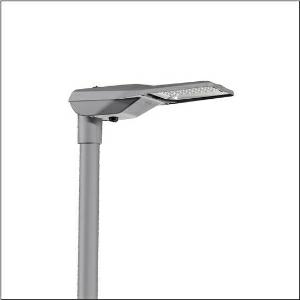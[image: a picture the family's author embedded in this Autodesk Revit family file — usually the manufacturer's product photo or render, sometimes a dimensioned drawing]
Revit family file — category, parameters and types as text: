
# Revit family: streetlight_sl_21_iq_mini___st0_8a_5xe2c31y08gb_e7ef
name_source: partatom
category: Lighting Fixtures
units: mm (PartAtom-declared; Revit-internal decimal feet)

## family parameters
Cut with Voids When Loaded = No
Host = Face
Light Source = No
Part Type = Normal
Room Calculation Point = No
Round Connector Dimension = Use Diameter
Shared = No

## types (1)
- --- (1 x LED, 5990 lm, 39.8 W, 3000K)
    Apparent Load = 40 VA
    CIE Flux Codes = 38 75 97 100 100
    Color Rendering = 70
    Color Temperature = 3000K
    Default Elevation = 1800 mm
    Description = Streetlight SL 21 iQ mini, mast luminaire, primary light control with lens, of PMMA, primary optical cover: cover, of toughened safety glass, transparent, light distribution: ST0.8a, light emission: direct distribution, primary light characteristic: asymmetric, installation type: post-top, side-entry, LED, High Power LED, rated luminous flux: 5.990lm, luminous efficacy: 151lm/W, light colour: 730, colour temperature: 3000K, control gear: iQ-Street Remote, D4i with power reduction, control: pre-setting: logarithmic dimming characteristic, Street-Remote, Auto-Match, Temp-Guard, Lumen-Switch, Night-Set, Smart-Wire, Light-Fading, Desk-Remote (wireless, voltage-free reading and setting of iQ features in the workshop via application-optimized NFC function/RFID function), optimised constant luminous flux control (CLO 2.0), mains connection: 220..240V, AC, 50/60Hz, start of lifetime: 40W, end of service life: 41W, reduction: 18W, luminaire housing, of diecast aluminium, powder-coated, Siteco® metallic grey (DB 702S), corrosivity category C5 mid according to DIN EN ISO 12944, please order mast flange separately, inclination adjustable: 0°, 5°, 10°, 15°, sealing non-destructively replaceable, multi-level sealing system, length: 628mm, width: 235mm, height: 110mm, mast flange for spigot size: 42mm (side-entry): 5XC10008XM4, 60/48mm (side-entry/post-top): 5XC10108XM2, 76/60mm (side-entry/post-top): 5XC10108XM1, mounting height: 4..8m, Smart Interface below and above, protection rating (complete): IP66, insulation class (complete): insulation class II (safety insulation), certification: CE, ENEC, ENEC+, VDE, impact resistance: IK10, permissible operating ambient temperature for outdoor applications: -40..+50°C, standard-compliant lighting for roads and squares, packaging unit: 1 piece

Light Distribution: ST0.8a
    Height = 110 mm
    Lamp = 1 x LED
    Lamp Light Flux = 5990 lm
    Lamp Power = 39.8 W
    Lamp count = 1
    Length = 625 mm
    Luminous efficacy = 151 lm/W
    Manufacturer = Siteco
    ModVariant = No
    Model = 5XE2C31Y08GB
    Number of Poles = 1
    OnlyDefault = Yes
    Power Factor = 1
    Product Name = Streetlight SL 21 iQ mini | ST0.8a
    Product group = mast luminaire | pylon top
    ProductGroupID = 6100
    Protection Class = Protection class II
    Protection Degree = IP 66
    RLX_Detail_Level = 1
    RLX_Emergency_Light_Flux = 0 lm
    RLX_Emergency_Type = 0
    RLX_Emergency_Type_DB = No
    RlxData = <blob elided: 92557 chars, md5=a2789c57>
    Socket = socket
    Standby Power = 0 W
    System Light Flux = 5990 lm
    System Power = 40 W
    Type Comments = factory setting: luminous flux: 100 % | dim-lin: 254 | 800 mA
    Type Image = l_1003514.jpg
    URL = http://relux.com
    VarID = @adj_134823
    Voltage = 0 V
    Weight = 0.00 kg
    Width = 234 mm

## geometry (parser evidence)
native form markers: Blend x4, Sweep x12
no freeform markers — native parametric forms only
